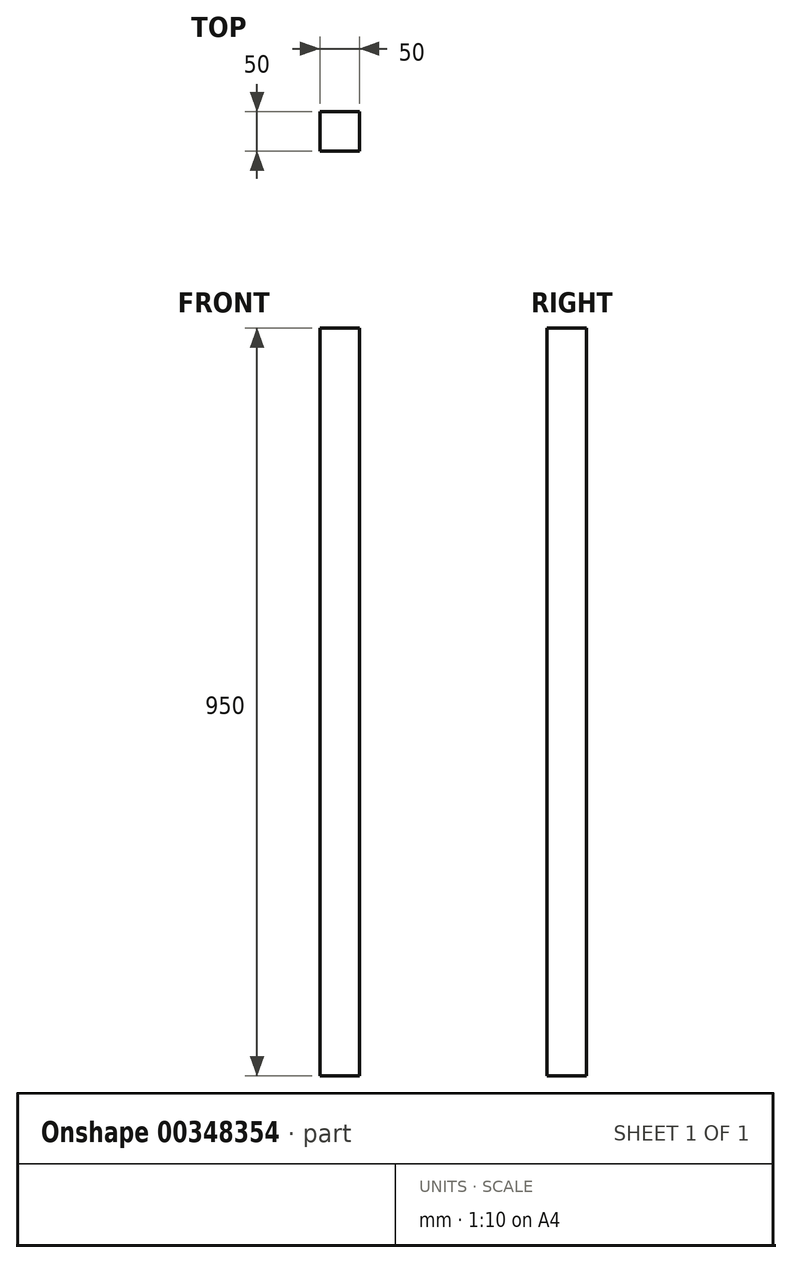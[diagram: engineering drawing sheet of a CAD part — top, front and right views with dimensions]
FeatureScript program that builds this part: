
annotation { "Feature Type Name" : "Feature", "Feature Type Description" : "" }
export const myFeature = defineFeature(function(context is Context, id is Id, definition is map)
    precondition{}
    {
        {
            var Q0;
            Q0=qCreatedBy(makeId("Top.planeOp"),FACE);
            var sketch = newSketch(context, id + "F0", { "sketchPlane" : qUnion([Q0])});
            skLineSegment(sketch, "E0.bottom", {"start": v(25, -25) * mm, "end": v(-25, -25) * mm});
            skLineSegment(sketch, "E0.top", {"start": v(25, 25) * mm, "end": v(-25, 25) * mm});
            skLineSegment(sketch, "E0.left", {"start": v(25, -25) * mm, "end": v(25, 25) * mm});
            skLineSegment(sketch, "E0.right", {"start": v(-25, -25) * mm, "end": v(-25, 25) * mm});
            skPoint(sketch, "E0.middle", {"position": v(0, 0) * mm});
            skSolve(sketch);
        }
        {
            var Q0;
            Q0=makeQuery(id+"F0.imprint","IMPRINT",FACE,{"disambiguationData":[TD([[makeQuery(id+"F0.imprint","IMPRINT",EDGE,{"derivedFrom":sQuery(id+"F0.wireOp",EDGE,"E0.bottom")}),-1.0]])]});
            extrude(context, id + "F1", {"entities" : qUnion([Q0]), "depth" : 950 * mm});
        }
    });
